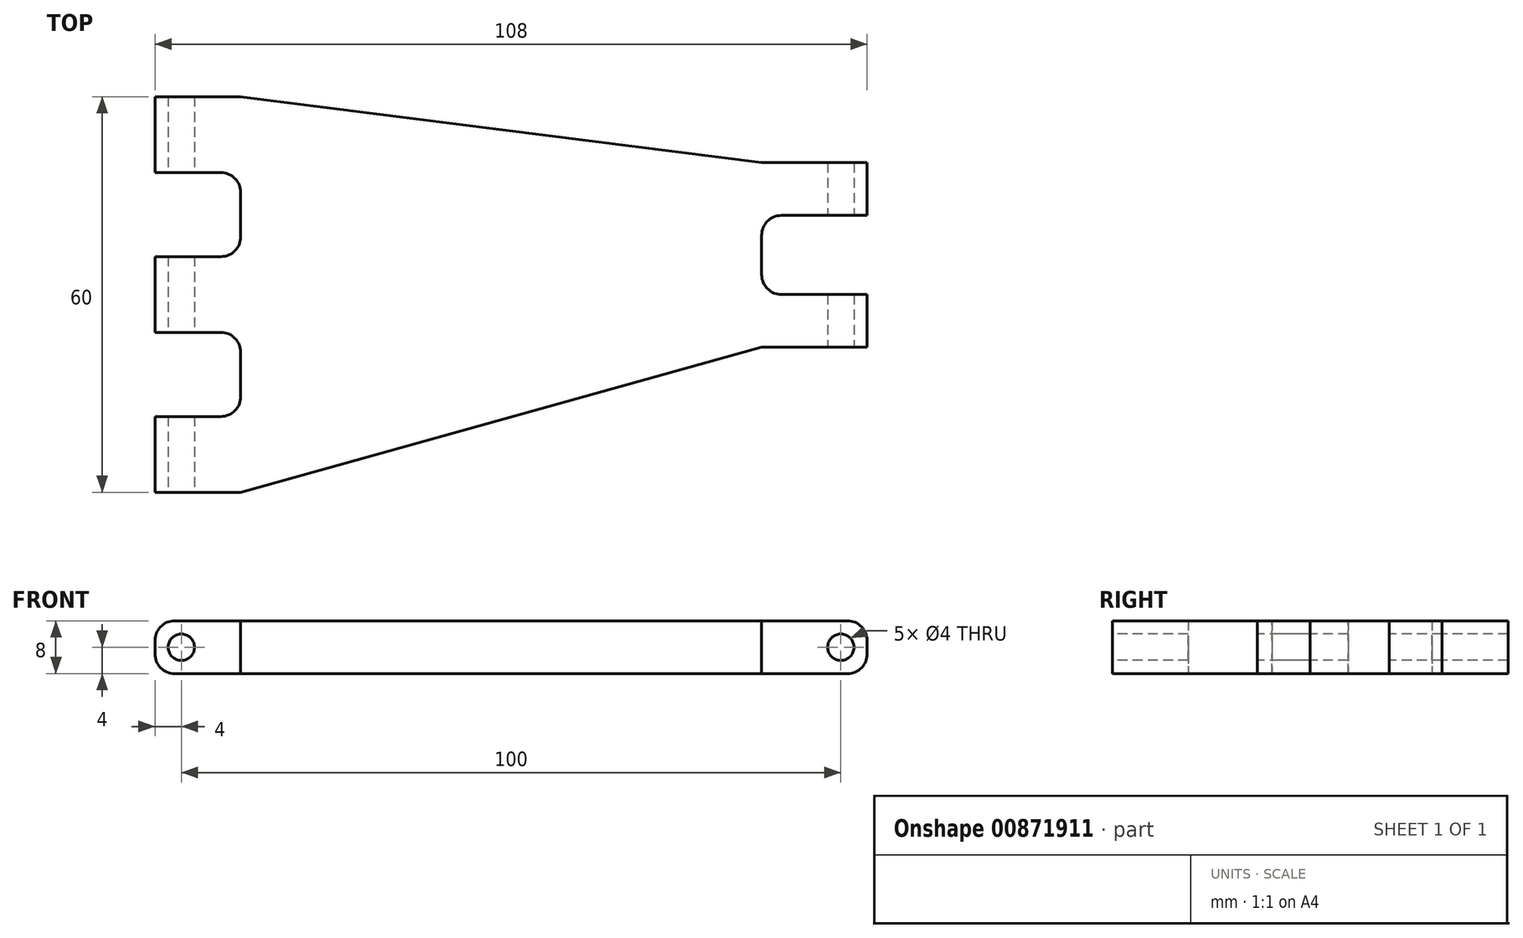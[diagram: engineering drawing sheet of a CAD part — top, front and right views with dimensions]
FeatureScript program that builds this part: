
annotation { "Feature Type Name" : "Feature", "Feature Type Description" : "" }
export const myFeature = defineFeature(function(context is Context, id is Id, definition is map)
    precondition{}
    {
        {
            var Q0;
            Q0=qCreatedBy(makeId("Top.planeOp"),FACE);
            var sketch = newSketch(context, id + "F0", { "sketchPlane" : qUnion([Q0])});
            skLineSegment(sketch, "E0.0", {"start": v(-4, 60) * mm, "end": v(-4, 48.5) * mm});
            skLineSegment(sketch, "E1.0", {"start": v(-4, 0) * mm, "end": v(-4, 11.5) * mm});
            skArc(sketch, "E2.0.0", {"start": v(6, 24.25) * mm, "mid": v(8.12, 23.37) * mm, "end": v(9, 21.25) * mm});
            skLineSegment(sketch, "E2.0.1", {"start": v(9, 21.25) * mm, "end": v(9, 14.5) * mm});
            skArc(sketch, "E2.0.2", {"start": v(9, 14.5) * mm, "mid": v(8.12, 12.38) * mm, "end": v(6, 11.5) * mm});
            skLineSegment(sketch, "E2.0.5", {"start": v(-4, 0) * mm, "end": v(9, 0) * mm});
            skArc(sketch, "E2.0.18", {"start": v(88, 39) * mm, "mid": v(88.88, 41.12) * mm, "end": v(91, 42) * mm});
            skLineSegment(sketch, "E2.0.21", {"start": v(104, 50) * mm, "end": v(88, 50) * mm});
            skLineSegment(sketch, "E3.0.3", {"start": v(6, 11.5) * mm, "end": v(-4, 11.5) * mm});
            skLineSegment(sketch, "E3.0.19", {"start": v(91, 42) * mm, "end": v(104, 42) * mm});
            skLineSegment(sketch, "E4.0.13", {"start": v(88, 22) * mm, "end": v(104, 22) * mm});
            skArc(sketch, "E4.0.16", {"start": v(91, 30) * mm, "mid": v(88.88, 30.88) * mm, "end": v(88, 33) * mm});
            skLineSegment(sketch, "E5", {"start": v(0, 0) * mm, "end": v(0, 65.17) * mm, "construction": true});
            skLineSegment(sketch, "E6", {"start": v(100, 65.3) * mm, "end": v(100, 5.57) * mm, "construction": true});
            skLineSegment(sketch, "E7", {"start": v(-4, 24.25) * mm, "end": v(6, 24.25) * mm});
            skLineSegment(sketch, "E8", {"start": v(104, 50) * mm, "end": v(104, 42) * mm});
            skLineSegment(sketch, "E9", {"start": v(104, 30) * mm, "end": v(104, 22) * mm});
            skLineSegment(sketch, "E10", {"start": v(100, 36) * mm, "end": v(135.8, 36) * mm, "construction": true});
            skLineSegment(sketch, "E11", {"start": v(88, 33) * mm, "end": v(88, 39) * mm});
            skLineSegment(sketch, "E12", {"start": v(91, 30) * mm, "end": v(104, 30) * mm});
            skLineSegment(sketch, "E13", {"start": v(9, 0) * mm, "end": v(88, 22) * mm});
            skLineSegment(sketch, "E14", {"start": v(-4, 60) * mm, "end": v(9, 60) * mm});
            skLineSegment(sketch, "E15", {"start": v(9, 60) * mm, "end": v(88, 50) * mm});
            skLineSegment(sketch, "E16", {"start": v(-4, 35.75) * mm, "end": v(6, 35.75) * mm});
            skLineSegment(sketch, "E17", {"start": v(9, 38.75) * mm, "end": v(9, 45.5) * mm});
            skLineSegment(sketch, "E18", {"start": v(6, 48.5) * mm, "end": v(-4, 48.5) * mm});
            skLineSegment(sketch, "E19.trimOffspring", {"start": v(-4, 35.75) * mm, "end": v(-4, 24.25) * mm});
            skPoint(sketch, "E20.visualSharp", {"position": v(9, 35.75) * mm});
            skArc(sketch, "E20.filletArc", {"start": v(6, 35.75) * mm, "mid": v(8.12, 36.63) * mm, "end": v(9, 38.75) * mm});
            skPoint(sketch, "E21.visualSharp", {"position": v(9, 48.5) * mm});
            skArc(sketch, "E21.filletArc", {"start": v(9, 45.5) * mm, "mid": v(8.12, 47.62) * mm, "end": v(6, 48.5) * mm});
            skLineSegment(sketch, "E22", {"start": v(-4, 30) * mm, "end": v(16.52, 30) * mm, "construction": true});
            skSolve(sketch);
        }
        {
            var Q0;
            Q0=makeQuery(id+"F0.imprint","IMPRINT",FACE,{"disambiguationData":[TD([[makeQuery(id+"F0.imprint","IMPRINT",EDGE,{"derivedFrom":sQuery(id+"F0.wireOp",EDGE,"E0.0")}),1.0]])]});
            extrude(context, id + "F1", {"entities" : qUnion([Q0]), "depth" : 8 * mm, "offsetDistance" : 25 * mm, "symmetric" : true});
        }
        {
            var Q0;
            Q0=makeQuery(id+"F1.opExtrude","SWEPT_FACE",FACE,{"disambiguationData":[OSD([sQuery(id+"F0.wireOp",EDGE,"E2.0.5"),sQuery(id+"F0.wireOp",EDGE,"E4.0.5")])]});
            var sketch = newSketch(context, id + "F2", { "sketchPlane" : qUnion([Q0])});
            skLineSegment(sketch, "E23", {"start": v(0, 0) * mm, "end": v(100, 0) * mm, "construction": true});
            skCircle(sketch, "E24", {"center": v(0, 0) * mm, "radius": 2 * mm});
            skCircle(sketch, "E25", {"center": v(100, 0) * mm, "radius": 2 * mm});
            skSolve(sketch);
        }
        {
            var Q0;
            Q0=qSketchRegion(id+"F2",true);
            extrude(context, id + "F3", {"entities" : qUnion([Q0]), "operationType" : NewBodyOperationType.REMOVE, "endBound" : BoundingType.THROUGH_ALL, "oppositeDirection" : true, "depth" : 25 * mm, "offsetDistance" : 25 * mm});
        }
        {
            var Q0;
            Q0=makeQuery(id+"F1.opExtrude","CAP_EDGE",EDGE,{"disambiguationData":[OSD([sQuery(id+"F0.wireOp",EDGE,"E1.0")])],"isStart":false});
            var Q1;
            Q1=makeQuery(id+"F1.opExtrude","CAP_EDGE",EDGE,{"disambiguationData":[OSD([sQuery(id+"F0.wireOp",EDGE,"E19.trimOffspring")])],"isStart":false});
            var Q2;
            Q2=makeQuery(id+"F1.opExtrude","CAP_EDGE",EDGE,{"disambiguationData":[OSD([sQuery(id+"F0.wireOp",EDGE,"E0.0")])],"isStart":false});
            var Q3;
            Q3=makeQuery(id+"F1.opExtrude","CAP_EDGE",EDGE,{"disambiguationData":[OSD([sQuery(id+"F0.wireOp",EDGE,"E1.0")])],"isStart":true});
            var Q4;
            Q4=makeQuery(id+"F1.opExtrude","CAP_EDGE",EDGE,{"disambiguationData":[OSD([sQuery(id+"F0.wireOp",EDGE,"E19.trimOffspring")])],"isStart":true});
            var Q5;
            Q5=makeQuery(id+"F1.opExtrude","CAP_EDGE",EDGE,{"disambiguationData":[OSD([sQuery(id+"F0.wireOp",EDGE,"E0.0")])],"isStart":true});
            var Q6;
            Q6=makeQuery(id+"F1.opExtrude","CAP_EDGE",EDGE,{"disambiguationData":[OSD([sQuery(id+"F0.wireOp",EDGE,"E8")])],"isStart":true});
            var Q7;
            Q7=makeQuery(id+"F1.opExtrude","CAP_EDGE",EDGE,{"disambiguationData":[OSD([sQuery(id+"F0.wireOp",EDGE,"E9")])],"isStart":true});
            var Q8;
            Q8=makeQuery(id+"F1.opExtrude","CAP_EDGE",EDGE,{"disambiguationData":[OSD([sQuery(id+"F0.wireOp",EDGE,"E9")])],"isStart":false});
            var Q9;
            Q9=makeQuery(id+"F1.opExtrude","CAP_EDGE",EDGE,{"disambiguationData":[OSD([sQuery(id+"F0.wireOp",EDGE,"E8")])],"isStart":false});
            fillet(context, id + "F4", {"entities" : qUnion([Q0, Q1, Q2, Q3, Q4, Q5, Q6, Q7, Q8, Q9]), "radius" : 3 * mm, "tangentPropagation" : true, "allowEdgeOverflow" : false});
        }
    });
